# Revit family: QF_ELECTROLUXPROFESSIONAL_391406_E9IIMAAOMIA
name_source: partatom
category: Specialty Equipment
units: mm (PartAtom-declared; Revit-internal decimal feet)

## family parameters
Always vertical = Yes
Cut with Voids When Loaded = No
Enable Cutting in Views = No
Maintain Annotation Orientation = No
Part Type = Normal
Room Calculation Point = No
Round Connector Dimension = Use Diameter
Shared = No
Work Plane-Based = No

## types (1)
- QF_ELECTROLUXPROFESSIONAL_391406_E9IIMAAOMIA
    Default Elevation = 0 mm  [stored 0 ft]
    Depth = 930 mm
    Description = GAS FRY TOP HP SMOOTH PLATE 1200 MM - SCRATCH RESISTANT CHROMIUM NITROCHROME3
    Direct Waste Size = 0"
    Gas Connection Height = 0 mm  [stored 0 ft]
    Gas Size = 1"
    HP = 0 HP
    Manufacturer = ELECTROLUX PROFESSIONAL
    Model = 391406
    URL = www.electrolux.com
    URL Cutsheet = www.electrolux.com
    Watts = 0 W
    Weight in Pounds = 150
    Width = 1200 mm  [stored 3.93701 ft]

note: [stored X ft] marks values corroborated as IEEE doubles in the binary element streams (Revit-internal decimal feet)

## geometry (parser evidence)
native form markers: Blend x20, Sweep x2
no freeform markers — native parametric forms only
